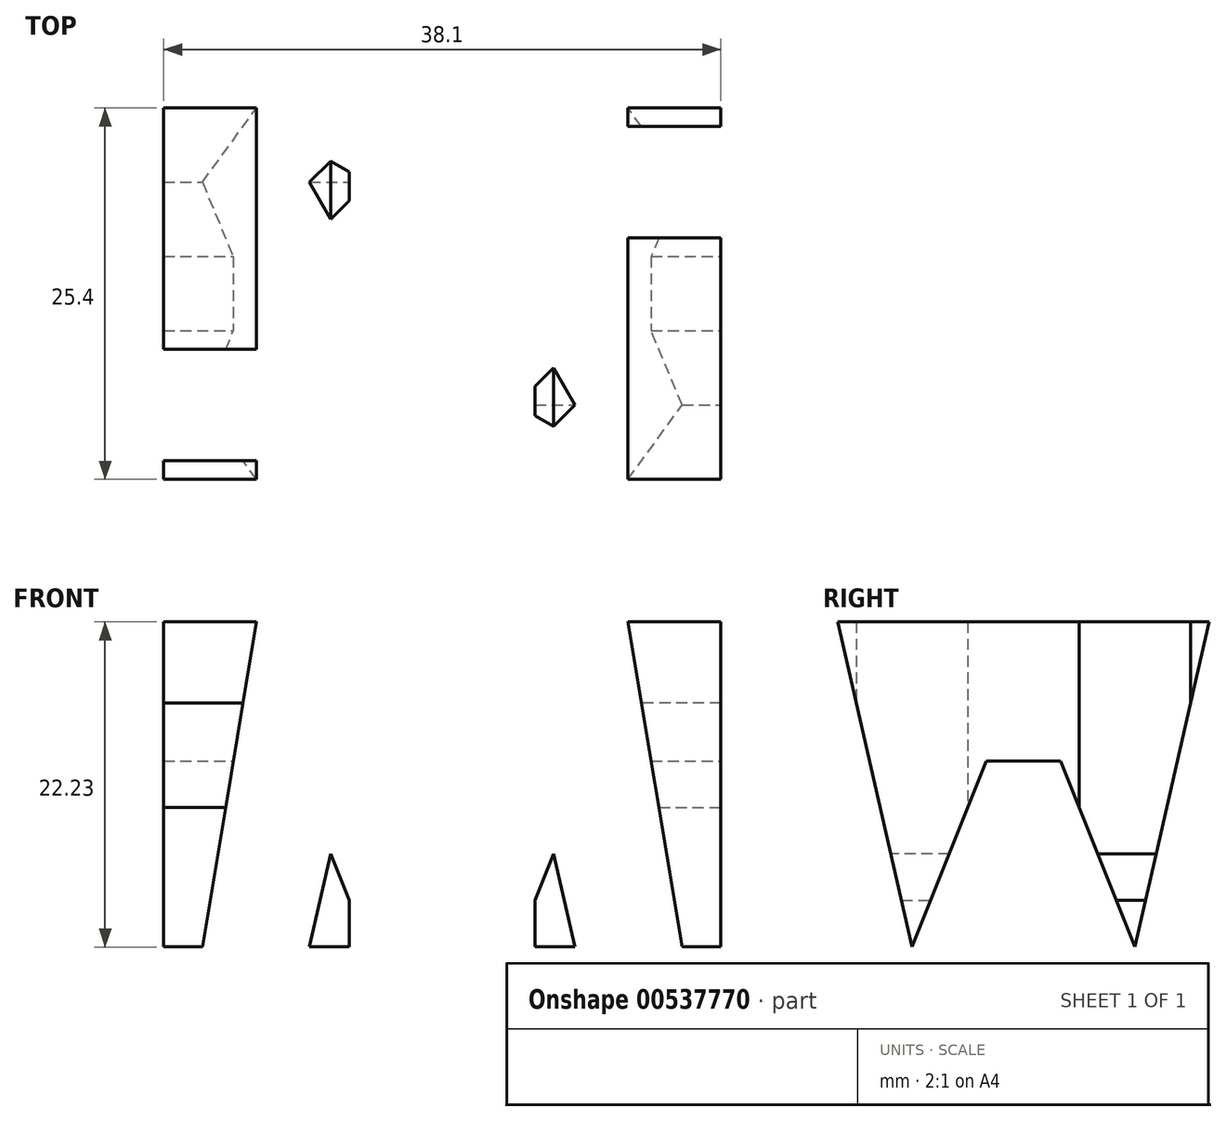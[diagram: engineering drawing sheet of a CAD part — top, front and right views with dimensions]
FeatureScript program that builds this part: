
annotation { "Feature Type Name" : "Feature", "Feature Type Description" : "" }
export const myFeature = defineFeature(function(context is Context, id is Id, definition is map)
    precondition{}
    {
        {
            var Q0;
            Q0=qCreatedBy(makeId("Front.planeOp"),FACE);
            var sketch = newSketch(context, id + "F0", { "sketchPlane" : qUnion([Q0])});
            skLineSegment(sketch, "E0.bottom", {"start": v(38.1, 38.1) * mm, "end": v(0, 38.1) * mm});
            skLineSegment(sketch, "E0.top", {"start": v(38.1, 0) * mm, "end": v(0, 0) * mm});
            skLineSegment(sketch, "E0.left", {"start": v(38.1, 38.1) * mm, "end": v(38.1, 0) * mm});
            skLineSegment(sketch, "E0.right", {"start": v(0, 38.1) * mm, "end": v(0, 0) * mm});
            skPoint(sketch, "E0.middle", {"position": v(0, 0) * mm});
            skSolve(sketch);
        }
        {
            var Q0;
            Q0 = qSketchRegion(id + "F0", true);
            extrude(context, id + "F1", {"entities" : qUnion([Q0]), "depth" : 38.1 * mm, "offsetDistance" : 25.4 * mm});
        }
        {
            var Q0;
            Q0=qCreatedBy(makeId("Front.planeOp"),FACE);
            cPlane(context, id + "F2", {"entities" : qUnion([Q0]), "cplaneType" : CPlaneType.OFFSET, "offset" : 38.1 * mm, "width" : 152.4 * mm, "height" : 152.4 * mm});
        }
        {
            var Q0;
            Q0=qCreatedBy(makeId("Right.planeOp"),FACE);
            cPlane(context, id + "F3", {"entities" : qUnion([Q0]), "cplaneType" : CPlaneType.OFFSET, "offset" : 38.1 * mm, "width" : 152.4 * mm, "height" : 152.4 * mm});
        }
        {
            var Q0;
            Q0=qCreatedBy(makeId("Top.planeOp"),FACE);
            cPlane(context, id + "F4", {"entities" : qUnion([Q0]), "cplaneType" : CPlaneType.OFFSET, "offset" : 38.1 * mm, "width" : 152.4 * mm, "height" : 152.4 * mm});
        }
        {
            var Q0;
            Q0=qCreatedBy(id+"F3.planeOp",FACE);
            var sketch = newSketch(context, id + "F5", { "sketchPlane" : qUnion([Q0])});
            skLineSegment(sketch, "E1.bottom", {"start": v(0, 0) * mm, "end": v(-38.1, 0) * mm});
            skLineSegment(sketch, "E1.top", {"start": v(0, 38.1) * mm, "end": v(-38.1, 38.1) * mm});
            skLineSegment(sketch, "E1.left", {"start": v(0, 0) * mm, "end": v(0, 38.1) * mm});
            skLineSegment(sketch, "E1.right", {"start": v(-38.1, 0) * mm, "end": v(-38.1, 38.1) * mm});
            skLineSegment(sketch, "E2", {"start": v(-25.4, 0) * mm, "end": v(-19.05, 15.88) * mm});
            skLineSegment(sketch, "E3", {"start": v(-19.05, 15.88) * mm, "end": v(-12.7, 0) * mm});
            skLineSegment(sketch, "E4", {"start": v(0, 38.1) * mm, "end": v(-6.35, 38.1) * mm});
            skLineSegment(sketch, "E5", {"start": v(-6.35, 38.1) * mm, "end": v(-11.43, 15.87) * mm});
            skLineSegment(sketch, "E6", {"start": v(-21.6, 28.58) * mm, "end": v(-26.67, 15.88) * mm});
            skLineSegment(sketch, "E7", {"start": v(-26.67, 15.88) * mm, "end": v(-31.75, 38.1) * mm});
            skLineSegment(sketch, "E8", {"start": v(-31.75, 38.1) * mm, "end": v(-38.1, 38.1) * mm});
            skLineSegment(sketch, "E9", {"start": v(-38.1, 38.1) * mm, "end": v(-31.75, 38.1) * mm});
            skLineSegment(sketch, "E10", {"start": v(-21.6, 28.58) * mm, "end": v(-16.51, 28.58) * mm});
            skLineSegment(sketch, "E11", {"start": v(-16.51, 28.58) * mm, "end": v(-11.43, 15.88) * mm});
            skLineSegment(sketch, "E12", {"start": v(0, 38.1) * mm, "end": v(-6.35, 0) * mm});
            skLineSegment(sketch, "E13", {"start": v(-6.35, 0) * mm, "end": v(-12.7, 0) * mm});
            skLineSegment(sketch, "E14", {"start": v(-38.1, 38.1) * mm, "end": v(-31.75, 0) * mm});
            skPoint(sketch, "E14.endSnap0", {"position": v(-34.93, 38.1) * mm});
            skLineSegment(sketch, "E15", {"start": v(-31.75, 0) * mm, "end": v(-25.4, 0) * mm});
            skLineSegment(sketch, "E16", {"start": v(-31.75, 0) * mm, "end": v(-38.1, 0) * mm});
            skSolve(sketch);
        }
        {
            var Q0;
            Q0=makeQuery(id+"F5.imprint","IMPRINT",FACE,{"disambiguationData":[TD([[makeQuery(id+"F5.imprint","IMPRINT",EDGE,{"derivedFrom":sQuery(id+"F5.wireOp",EDGE,"E1.right")}),-1.0]])]});
            var Q1;
            Q1=makeQuery(id+"F5.imprint","IMPRINT",FACE,{"disambiguationData":[TD([[makeQuery(id+"F5.imprint","IMPRINT",EDGE,{"derivedFrom":sQuery(id+"F5.wireOp",EDGE,"E1.top")}),1.0]])]});
            var Q2;
            {var subQ0=sQuery(id+"F5.wireOp",EDGE,"E2");Q2=makeQuery(id+"F5.imprint","IMPRINT",FACE,{"disambiguationData":[TD([[makeQuery(id+"F5.imprint","IMPRINT",EDGE,{"derivedFrom":subQ0}),-1.0]])]});}
            var Q3;
            {var subQ0=sQuery(id+"F5.wireOp",EDGE,"E1.left");Q3=makeQuery(id+"F5.imprint","IMPRINT",FACE,{"disambiguationData":[TD([[makeQuery(id+"F5.imprint","IMPRINT",EDGE,{"derivedFrom":subQ0}),1.0]])]});}
            extrude(context, id + "F6", {"entities" : qUnion([Q0, Q1, Q2, Q3]), "operationType" : NewBodyOperationType.REMOVE, "oppositeDirection" : true, "depth" : 38.1 * mm, "offsetDistance" : 25.4 * mm});
        }
        {
            var Q0;
            Q0=qCreatedBy(id+"F2.planeOp",FACE);
            var sketch = newSketch(context, id + "F7", { "sketchPlane" : qUnion([Q0])});
            skLineSegment(sketch, "E17.bottom", {"start": v(0, 0) * mm, "end": v(38.1, 0) * mm});
            skLineSegment(sketch, "E17.top", {"start": v(0, 38.1) * mm, "end": v(38.1, 38.1) * mm});
            skLineSegment(sketch, "E17.left", {"start": v(0, 0) * mm, "end": v(0, 38.1) * mm});
            skLineSegment(sketch, "E17.right", {"start": v(38.1, 0) * mm, "end": v(38.1, 38.1) * mm});
            skLineSegment(sketch, "E18.left", {"start": v(0, 38.1) * mm, "end": v(0, 0) * mm});
            skLineSegment(sketch, "E18.right", {"start": v(38.1, 38.1) * mm, "end": v(38.1, 0) * mm});
            skLineSegment(sketch, "E19", {"start": v(25.4, 38.1) * mm, "end": v(19.05, 22.22) * mm});
            skLineSegment(sketch, "E20", {"start": v(19.05, 22.22) * mm, "end": v(12.7, 38.1) * mm});
            skLineSegment(sketch, "E21", {"start": v(0, 0) * mm, "end": v(6.35, 0) * mm});
            skLineSegment(sketch, "E22", {"start": v(6.35, 0) * mm, "end": v(11.43, 22.23) * mm});
            skLineSegment(sketch, "E23", {"start": v(21.59, 9.52) * mm, "end": v(26.67, 22.22) * mm});
            skLineSegment(sketch, "E24", {"start": v(26.67, 22.23) * mm, "end": v(31.75, 0) * mm});
            skLineSegment(sketch, "E25", {"start": v(31.75, 0) * mm, "end": v(38.1, 0) * mm});
            skLineSegment(sketch, "E26", {"start": v(38.1, 0) * mm, "end": v(31.75, 0) * mm});
            skLineSegment(sketch, "E27", {"start": v(21.59, 9.52) * mm, "end": v(16.5, 9.52) * mm});
            skLineSegment(sketch, "E28", {"start": v(16.51, 9.52) * mm, "end": v(11.43, 22.23) * mm});
            skLineSegment(sketch, "E29", {"start": v(0, 0) * mm, "end": v(6.35, 38.1) * mm});
            skLineSegment(sketch, "E30", {"start": v(6.35, 38.1) * mm, "end": v(12.7, 38.1) * mm});
            skLineSegment(sketch, "E31", {"start": v(38.1, 0) * mm, "end": v(31.75, 38.1) * mm});
            skPoint(sketch, "E31.endSnap0", {"position": v(34.92, 0) * mm});
            skLineSegment(sketch, "E32", {"start": v(31.75, 38.1) * mm, "end": v(25.4, 38.1) * mm});
            skLineSegment(sketch, "E33", {"start": v(31.75, 38.1) * mm, "end": v(38.1, 38.1) * mm});
            skSolve(sketch);
        }
        {
            var Q0;
            Q0=makeQuery(id+"F7.imprint","IMPRINT",FACE,{"disambiguationData":[TD([[makeQuery(id+"F7.imprint","IMPRINT",EDGE,{"derivedFrom":sQuery(id+"F7.wireOp",EDGE,"E17.bottom")}),1.0]])]});
            var Q1;
            Q1=makeQuery(id+"F7.imprint","IMPRINT",FACE,{"disambiguationData":[TD([[makeQuery(id+"F7.imprint","IMPRINT",EDGE,{"derivedFrom":sQuery(id+"F7.wireOp",EDGE,"E18.right")}),-1.0]])]});
            var Q2;
            {var subQ0=sQuery(id+"F7.wireOp",EDGE,"E19");Q2=makeQuery(id+"F7.imprint","IMPRINT",FACE,{"disambiguationData":[TD([[makeQuery(id+"F7.imprint","IMPRINT",EDGE,{"derivedFrom":subQ0}),-1.0]])]});}
            var Q3;
            {var subQ0=sQuery(id+"F7.wireOp",EDGE,"E18.left");Q3=makeQuery(id+"F7.imprint","IMPRINT",FACE,{"disambiguationData":[TD([[makeQuery(id+"F7.imprint","IMPRINT",EDGE,{"derivedFrom":subQ0}),1.0]])]});}
            extrude(context, id + "F8", {"entities" : qUnion([Q0, Q1, Q2, Q3]), "operationType" : NewBodyOperationType.REMOVE, "oppositeDirection" : true, "depth" : 38.1 * mm, "offsetDistance" : 25.4 * mm});
        }
        {
            var Q0;
            Q0=qCreatedBy(id+"F4.planeOp",FACE);
            var sketch = newSketch(context, id + "F9", { "sketchPlane" : qUnion([Q0])});
            skLineSegment(sketch, "E34.bottom", {"start": v(0, 0) * mm, "end": v(38.1, 0) * mm});
            skLineSegment(sketch, "E34.top", {"start": v(0, -38.1) * mm, "end": v(38.1, -38.1) * mm});
            skLineSegment(sketch, "E34.left", {"start": v(0, 0) * mm, "end": v(0, -38.1) * mm});
            skLineSegment(sketch, "E34.right", {"start": v(38.1, 0) * mm, "end": v(38.1, -38.1) * mm});
            skLineSegment(sketch, "E35.bottom", {"start": v(38.1, -7.62) * mm, "end": v(12.7, -7.62) * mm});
            skLineSegment(sketch, "E35.top", {"start": v(38.1, -15.24) * mm, "end": v(12.7, -15.24) * mm});
            skLineSegment(sketch, "E35.left", {"start": v(38.1, -7.62) * mm, "end": v(38.1, -15.24) * mm});
            skLineSegment(sketch, "E35.right", {"start": v(12.7, -7.62) * mm, "end": v(12.7, -15.24) * mm});
            skLineSegment(sketch, "E36.bottom", {"start": v(0, -22.86) * mm, "end": v(25.4, -22.86) * mm});
            skLineSegment(sketch, "E36.top", {"start": v(0, -30.48) * mm, "end": v(25.4, -30.48) * mm});
            skLineSegment(sketch, "E36.left", {"start": v(0, -22.86) * mm, "end": v(0, -30.48) * mm});
            skLineSegment(sketch, "E36.right", {"start": v(25.4, -22.86) * mm, "end": v(25.4, -30.48) * mm});
            skSolve(sketch);
        }
        {
            var Q0;
            Q0=makeQuery(id+"F9.imprint","IMPRINT",FACE,{"disambiguationData":[TD([[makeQuery(id+"F9.imprint","IMPRINT",EDGE,{"derivedFrom":sQuery(id+"F9.wireOp",EDGE,"E35.bottom")}),1.0]])]});
            var Q1;
            Q1=makeQuery(id+"F9.imprint","IMPRINT",FACE,{"disambiguationData":[TD([[makeQuery(id+"F9.imprint","IMPRINT",EDGE,{"derivedFrom":sQuery(id+"F9.wireOp",EDGE,"E36.bottom")}),-1.0]])]});
            extrude(context, id + "F10", {"entities" : qUnion([Q0, Q1]), "operationType" : NewBodyOperationType.REMOVE, "oppositeDirection" : true, "depth" : 38.1 * mm, "offsetDistance" : 25.4 * mm});
        }
    });
